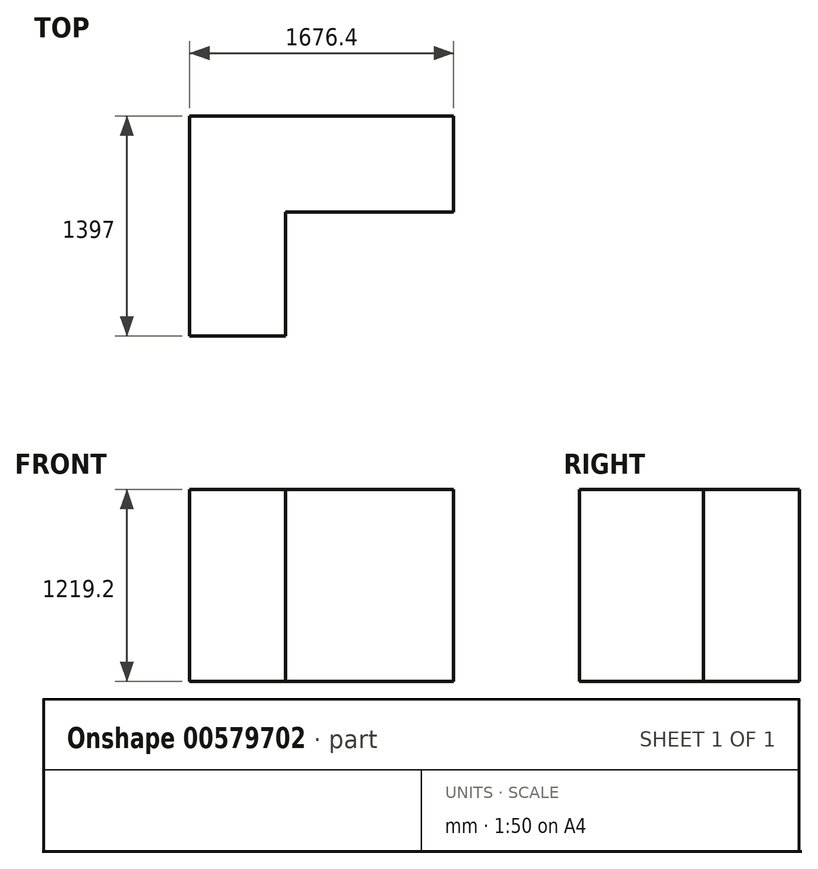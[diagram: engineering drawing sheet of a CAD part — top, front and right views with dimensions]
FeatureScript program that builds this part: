
annotation { "Feature Type Name" : "Feature", "Feature Type Description" : "" }
export const myFeature = defineFeature(function(context is Context, id is Id, definition is map)
    precondition{}
    {
        {
            var Q0;
            Q0=qCreatedBy(makeId("Top.planeOp"),FACE);
            var sketch = newSketch(context, id + "F0", { "sketchPlane" : qUnion([Q0])});
            skLineSegment(sketch, "E0", {"start": v(0, 0) * mm, "end": v(0, 1397) * mm});
            skLineSegment(sketch, "E1", {"start": v(0, 1397) * mm, "end": v(1676.4, 1397) * mm});
            skLineSegment(sketch, "E2", {"start": v(1676.4, 1397) * mm, "end": v(1676.4, 787.4) * mm});
            skLineSegment(sketch, "E3", {"start": v(1676.4, 787.4) * mm, "end": v(609.6, 787.4) * mm});
            skLineSegment(sketch, "E4", {"start": v(609.6, 787.4) * mm, "end": v(609.6, 0) * mm});
            skLineSegment(sketch, "E5", {"start": v(609.6, 0) * mm, "end": v(0, 0) * mm});
            skSolve(sketch);
        }
        {
            var Q0;
            Q0=makeQuery(id+"F0.imprint","IMPRINT",FACE,{"disambiguationData":[TD([[makeQuery(id+"F0.imprint","IMPRINT",EDGE,{"derivedFrom":sQuery(id+"F0.wireOp",EDGE,"E0")}),-1.0]])]});
            extrude(context, id + "F1", {"entities" : qUnion([Q0]), "depth" : 1219.2 * mm, "offsetDistance" : 25.4 * mm});
        }
    });
